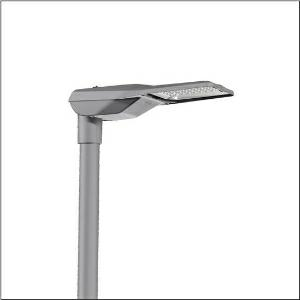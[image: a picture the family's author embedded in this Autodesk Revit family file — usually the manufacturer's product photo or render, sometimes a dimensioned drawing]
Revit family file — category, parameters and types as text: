
# Revit family: streetlight_sl_21_mini___st1_0a_5xe2d43s08gb_5b06
name_source: partatom
category: Lighting Fixtures
units: mm (PartAtom-declared; Revit-internal decimal feet)

## family parameters
Cut with Voids When Loaded = No
Host = Face
Light Source = No
Part Type = Normal
Room Calculation Point = No
Round Connector Dimension = Use Diameter
Shared = No

## types (1)
- --- (1 x LED, 6180 lm, 40.4 W, 4000K)
    Apparent Load = 40 VA
    CIE Flux Codes = 37 72 97 100 100
    Color Rendering = 70
    Color Temperature = 4000K
    Default Elevation = 1800 mm
    Description = Streetlight SL 21 mini, mast luminaire, primary light control with lens, of PMMA, primary optical cover: cover, of toughened safety glass, transparent, light distribution: ST1.0a, light emission: direct distribution, primary light characteristic: asymmetric, installation type: side-entry, post-top, LED, High Power LED, rated luminous flux: 6.180lm, luminous efficacy: 153lm/W, light colour: 740, colour temperature: 4000K, control gear: D4i, control: overheat protection, constant luminous flux control, time-dependent luminous flux control, flexible luminous flux parameterisation, pre-setting: logarithmic dimming characteristic, mains connection: 220..240V, AC, 50/60Hz, start of lifetime: 40W, end of service life: 41W, reduction: 19W, luminaire housing, of diecast aluminium, powder-coated, SITECO metallic grey (DB 702S), corrosivity category C5 high according to DIN EN ISO 12944, please order mast flange separately, inclination adjustable: 0°, 5°, 10°, 15°, sealing non-destructively replaceable, multi-level sealing system, length: 628mm, width: 235mm, height: 110mm, mast flange for spigot size: 42mm (side-entry): 5XC10008XM4, 60/48mm (side-entry/post-top): 5XC10108XM2, 76/60mm (side-entry/post-top): 5XC10108XM1, mounting height: 4..8m, Smart Interface above, protection rating (complete): IP66, insulation class (complete): insulation class II (safety insulation), certification: CE, ENEC, ENEC+, VDE, impact resistance: IK10, permissible operating ambient temperature for outdoor applications: -40..+50°C, standard-compliant lighting for roads and squares, packaging unit: 1 piece

Light Distribution: ST1.0a
    Height = 110 mm
    Lamp = 1 x LED
    Lamp Light Flux = 6180 lm
    Lamp Power = 40.4 W
    Lamp count = 1
    Length = 625 mm
    Luminous efficacy = 153 lm/W
    Manufacturer = Siteco
    ModVariant = No
    Model = 5XE2D43S08GB
    Number of Poles = 1
    OnlyDefault = Yes
    Power Factor = 1
    Product Name = Streetlight SL 21 mini | ST1.0a
    Product group = mast luminaire | pylon top
    ProductGroupID = 6100
    Protection Class = Protection class II
    Protection Degree = IP 66
    RLX_Detail_Level = 1
    RLX_Emergency_Light_Flux = 0 lm
    RLX_Emergency_Type = 0
    RLX_Emergency_Type_DB = No
    RlxData = <blob elided: 26093 chars, md5=130e5c05>
    Socket = socket
    Standby Power = 0 W
    System Light Flux = 6180 lm
    System Power = 40 W
    Type Comments = factory setting: luminous flux: 100 % | dim-lin: 254 | 812 mA
    Type Image = l_1003515.jpg
    URL = http://relux.com
    VarID = @adj_186155
    Voltage = 0 V
    Weight = 0.00 kg
    Width = 234 mm

## geometry (parser evidence)
native form markers: Blend x4, Sweep x10
no freeform markers — native parametric forms only
